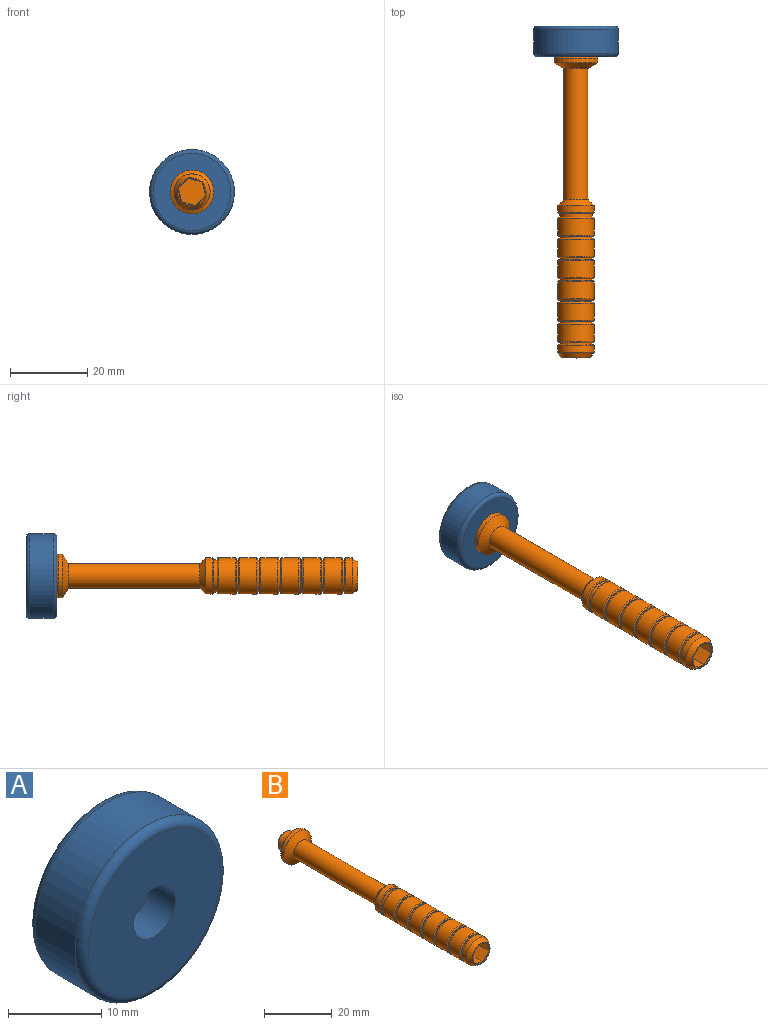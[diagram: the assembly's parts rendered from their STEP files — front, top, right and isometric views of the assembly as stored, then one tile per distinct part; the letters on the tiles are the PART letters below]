
ASSEMBLY  parts=2 mates=1
PART A: 7 faces, bbox 23.8x8x23.8 mm
  f0: cylinder r=3.17mm len=6.35mm, axis (0,1,0), area 79.8mm2, adj f2,f4
  f1: cylinder r=11mm len=22mm, axis (0,1,0), area 414.7mm2, adj f5,f6
  f2: plane 20x20mm, normal (0,-1,0), area 282.5mm2, adj f0,f6
  f3: plane 20x20mm, normal (0,1,0), area 314.2mm2, adj f5
  f4: plane 6.35x6.35mm, normal (0,-1,0), area 31.7mm2, adj f0
  f5: torus R=10mm, axis (0,-1,0), area 105mm2, adj f1,f3
  f6: torus R=10mm, axis (0,-1,0), area 105mm2, adj f1,f2
PART B: 72 faces, bbox 12.3x82x12.3 mm
  f0: plane 2.83x0.74mm, normal (0,-1,0), area 0.6mm2, adj f42,f71
  f1: plane 2.79x0.85mm, normal (0,-1,0), area 0.6mm2, adj f42,f69
  f2: plane 2.11x2.01mm, normal (0,-1,0), area 0.6mm2, adj f42,f67
  f3: plane 2.83x0.74mm, normal (0,-1,0), area 0.6mm2, adj f42,f66
  f4: plane 2.79x0.85mm, normal (0,-1,0), area 0.6mm2, adj f42,f68
  f5: plane 2.11x2.01mm, normal (0,-1,0), area 0.6mm2, adj f42,f70
  f6: plane 5.35x5.35mm, normal (0,1,0), area 22.5mm2, adj f58
  f7: cylinder r=3.17mm len=6.35mm, axis (0,1,0), area 69.8mm2, adj f8,f58
  f8: plane 10.75x10.75mm, normal (0,1,0), area 59.1mm2, adj f7,f57
  f9: cylinder r=5.68mm len=11.35mm, axis (0,1,0), area 42.8mm2, adj f10,f57
  f10: cone r=5.68mm half-angle=59deg, axis (0,1,0), area 81.1mm2, adj f9,f11
  f11: cylinder r=3.17mm len=34mm, axis (0,1,0), area 678.3mm2, adj f10,f12
  f12: cone r=3.17mm half-angle=45deg, axis (0,-1,0), area 52.3mm2, adj f11,f13
  f13: cylinder r=4.68mm len=9.35mm, axis (0,1,0), area 49.9mm2, adj f12,f43
  f14: plane 8.75x8.75mm, normal (0,-1,0), area 5.4mm2, adj f15,f43
  f15: cylinder r=4.17mm len=8.35mm, axis (0,1,0), area 26.2mm2, adj f14,f16
  f16: plane 8.75x8.75mm, normal (0,1,0), area 5.4mm2, adj f15,f44
  f17: cylinder r=4.68mm len=9.35mm, axis (0,1,0), area 129.2mm2, adj f44,f45
  f18: plane 8.75x8.75mm, normal (0,-1,0), area 5.4mm2, adj f19,f45
  f19: cylinder r=4.17mm len=8.35mm, axis (0,1,0), area 13.1mm2, adj f18,f20
  f20: plane 8.75x8.75mm, normal (0,1,0), area 5.4mm2, adj f19,f46
  f21: cylinder r=4.68mm len=9.35mm, axis (0,1,0), area 129.2mm2, adj f46,f47
  f22: plane 8.75x8.75mm, normal (0,-1,0), area 5.4mm2, adj f23,f47
  f23: cylinder r=4.17mm len=8.35mm, axis (0,1,0), area 13.1mm2, adj f22,f24
  f24: plane 8.75x8.75mm, normal (0,1,0), area 5.4mm2, adj f23,f48
  f25: cylinder r=4.68mm len=9.35mm, axis (0,1,0), area 129.2mm2, adj f48,f49
  f26: plane 8.75x8.75mm, normal (0,-1,0), area 5.4mm2, adj f27,f49
  f27: cylinder r=4.17mm len=8.35mm, axis (0,1,0), area 13.1mm2, adj f26,f28
  f28: plane 8.75x8.75mm, normal (0,1,0), area 5.4mm2, adj f27,f50
  f29: cylinder r=4.68mm len=9.35mm, axis (0,1,0), area 129.2mm2, adj f50,f51
  f30: plane 8.75x8.75mm, normal (0,-1,0), area 5.4mm2, adj f31,f51
  f31: cylinder r=4.17mm len=8.35mm, axis (0,1,0), area 13.1mm2, adj f30,f32
  f32: plane 8.75x8.75mm, normal (0,1,0), area 5.4mm2, adj f31,f52
  f33: cylinder r=4.68mm len=9.35mm, axis (0,1,0), area 129.2mm2, adj f52,f53
  f34: plane 8.75x8.75mm, normal (0,-1,0), area 5.4mm2, adj f35,f53
  f35: cylinder r=4.17mm len=8.35mm, axis (0,1,0), area 13.1mm2, adj f34,f36
  f36: plane 8.75x8.75mm, normal (0,1,0), area 5.4mm2, adj f35,f54
  f37: cylinder r=4.68mm len=9.35mm, axis (0,1,0), area 129.2mm2, adj f54,f55
  f38: plane 8.75x8.75mm, normal (0,-1,0), area 5.4mm2, adj f39,f55
  f39: cylinder r=4.17mm len=8.35mm, axis (0,1,0), area 13.1mm2, adj f38,f40
  f40: plane 8.75x8.75mm, normal (0,1,0), area 5.4mm2, adj f39,f56
  f41: cylinder r=4.68mm len=9.35mm, axis (0,1,0), area 49.9mm2, adj f42,f56
  f42: cone r=4.68mm half-angle=33.7deg, axis (0,1,0), area 46.9mm2, adj f0,f1,f2,f3,f4,f5,f41,f66
  f43: torus R=4.38mm, axis (0,-1,0), area 13.5mm2, adj f13,f14
  f44: torus R=4.38mm, axis (0,1,0), area 13.5mm2, adj f16,f17
  f45: torus R=4.38mm, axis (0,-1,0), area 13.5mm2, adj f17,f18
  f46: torus R=4.38mm, axis (0,1,0), area 13.5mm2, adj f20,f21
  f47: torus R=4.38mm, axis (0,-1,0), area 13.5mm2, adj f21,f22
  f48: torus R=4.38mm, axis (0,1,0), area 13.5mm2, adj f24,f25
  f49: torus R=4.38mm, axis (0,-1,0), area 13.5mm2, adj f25,f26
  f50: torus R=4.38mm, axis (0,1,0), area 13.5mm2, adj f28,f29
  f51: torus R=4.38mm, axis (0,-1,0), area 13.5mm2, adj f29,f30
  f52: torus R=4.38mm, axis (0,1,0), area 13.5mm2, adj f32,f33
  f53: torus R=4.38mm, axis (0,-1,0), area 13.5mm2, adj f33,f34
  f54: torus R=4.38mm, axis (0,1,0), area 13.5mm2, adj f36,f37
  f55: torus R=4.38mm, axis (0,-1,0), area 13.5mm2, adj f37,f38
  f56: torus R=4.38mm, axis (0,1,0), area 13.5mm2, adj f40,f41
  f57: torus R=5.38mm, axis (0,1,0), area 16.5mm2, adj f8,f9
  f58: cone r=2.67mm half-angle=45deg, axis (0,-1,0), area 13mm2, adj f6,f7
  f59: plane 7.8x2.66mm, normal (-0.69,0,0.72), area 28.6mm2, adj f60,f64,f65,f67
  f60: plane 7.8x3.56mm, normal (-0.97,0,-0.24), area 28.6mm2, adj f59,f61,f65,f66
  f61: plane 7.8x3.52mm, normal (-0.28,0,-0.96), area 28.6mm2, adj f60,f62,f65,f68
  f62: plane 7.8x2.66mm, normal (0.69,0,-0.72), area 28.6mm2, adj f61,f63,f65,f70
  f63: plane 7.8x3.56mm, normal (0.97,0,0.24), area 28.6mm2, adj f62,f64,f65,f71
  f64: plane 7.8x3.52mm, normal (0.28,0,0.96), area 28.6mm2, adj f59,f63,f65,f69
  f65: plane 7.13x7.03mm, normal (0,-1,0), area 34.9mm2, adj f59,f60,f61,f62,f63,f64
  f66: plane 3.66x0.98mm, normal (-0.69,-0.71,-0.17), area 1mm2, adj f3,f42,f60,f67,f68
  f67: plane 2.75x2.63mm, normal (-0.49,-0.71,0.51), area 1mm2, adj f2,f42,f59,f66,f69
  f68: plane 3.61x1.13mm, normal (-0.2,-0.71,-0.68), area 1mm2, adj f4,f42,f61,f66,f70
  f69: plane 3.61x1.13mm, normal (0.2,-0.71,0.68), area 1mm2, adj f1,f42,f64,f67,f71
  f70: plane 2.75x2.63mm, normal (0.49,-0.71,-0.51), area 1mm2, adj f5,f42,f62,f68,f71
  f71: plane 3.66x0.98mm, normal (0.69,-0.71,0.17), area 1mm2, adj f0,f42,f63,f69,f70
PLACE A t=(-36.41,-20.65,-5.44)mm
PLACE B t=(-36.41,-24.65,-5.44)mm
MATE fastened B.f58 <-> A.f1  axis (0,1,0) through (-36.41,-24.65,-5.44)mm
